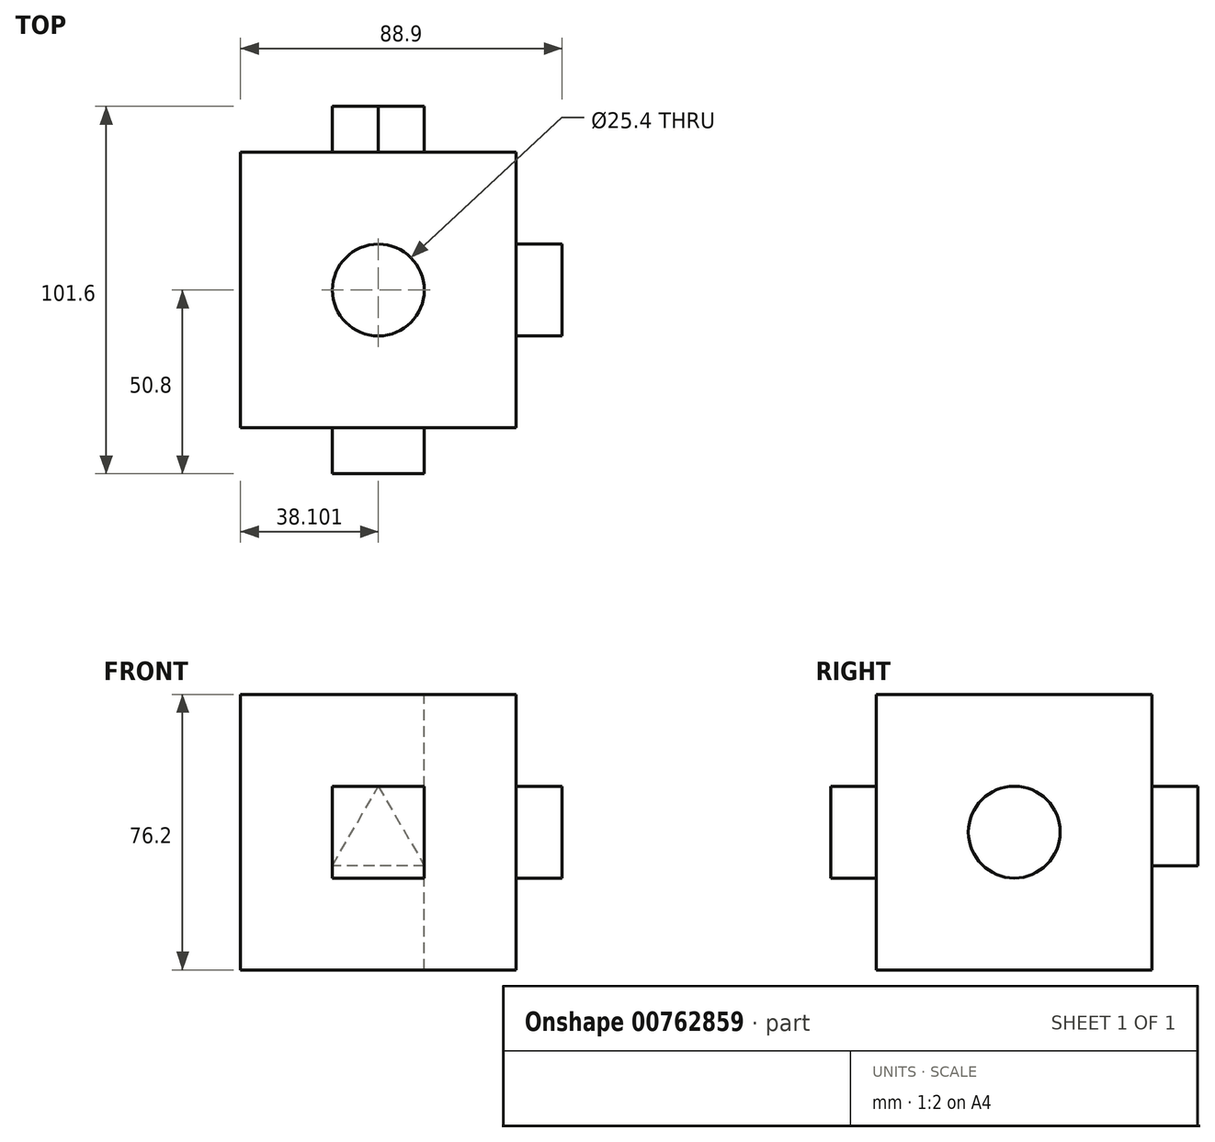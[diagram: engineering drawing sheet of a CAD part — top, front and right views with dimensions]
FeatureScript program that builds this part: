
annotation { "Feature Type Name" : "Feature", "Feature Type Description" : "" }
export const myFeature = defineFeature(function(context is Context, id is Id, definition is map)
    precondition{}
    {
        {
            var Q0;
            Q0=qCreatedBy(makeId("Front.planeOp"),FACE);
            var sketch = newSketch(context, id + "F0", { "sketchPlane" : qUnion([Q0])});
            skLineSegment(sketch, "E0.bottom", {"start": v(-73.54, 74.26) * mm, "end": v(2.66, 74.26) * mm});
            skLineSegment(sketch, "E0.top", {"start": v(-73.54, -1.94) * mm, "end": v(2.66, -1.94) * mm});
            skLineSegment(sketch, "E0.left", {"start": v(-73.54, 74.26) * mm, "end": v(-73.54, -1.94) * mm});
            skLineSegment(sketch, "E0.right", {"start": v(2.66, 74.26) * mm, "end": v(2.66, -1.94) * mm});
            skSolve(sketch);
        }
        {
            var Q0;
            Q0=makeQuery(id+"F0.imprint","IMPRINT",FACE,{"disambiguationData":[TD([[makeQuery(id+"F0.imprint","IMPRINT",EDGE,{"derivedFrom":sQuery(id+"F0.wireOp",EDGE,"E0.bottom")}),-1.0]])]});
            extrude(context, id + "F1", {"entities" : qUnion([Q0]), "depth" : 76.2 * mm, "offsetDistance" : 25.4 * mm});
        }
        {
            var Q0;
            Q0=makeQuery(id+"F1.opExtrude","CAP_FACE",FACE,{"disambiguationData":[OSD([sQuery(id+"F0.wireOp",EDGE,"E0.bottom"),sQuery(id+"F0.wireOp",EDGE,"E0.top"),sQuery(id+"F0.wireOp",EDGE,"E0.left"),sQuery(id+"F0.wireOp",EDGE,"E0.right")])],"isStart":false});
            var sketch = newSketch(context, id + "F2", { "sketchPlane" : qUnion([Q0])});
            skLineSegment(sketch, "E1.bottom", {"start": v(-48.14, 48.86) * mm, "end": v(-22.74, 48.86) * mm});
            skLineSegment(sketch, "E1.top", {"start": v(-48.14, 23.46) * mm, "end": v(-22.74, 23.46) * mm});
            skLineSegment(sketch, "E1.left", {"start": v(-48.14, 48.86) * mm, "end": v(-48.14, 23.46) * mm});
            skLineSegment(sketch, "E1.right", {"start": v(-22.74, 48.86) * mm, "end": v(-22.74, 23.46) * mm});
            skSolve(sketch);
        }
        {
            var Q0;
            Q0=makeQuery(id+"F2.imprint","IMPRINT",FACE,{"disambiguationData":[TD([[makeQuery(id+"F2.imprint","IMPRINT",EDGE,{"derivedFrom":sQuery(id+"F2.wireOp",EDGE,"E1.bottom")}),-1.0]])]});
            extrude(context, id + "F3", {"entities" : qUnion([Q0]), "operationType" : NewBodyOperationType.ADD, "depth" : 12.7 * mm, "offsetDistance" : 25.4 * mm});
        }
        {
            var Q0;
            Q0=makeQuery(id+"F1.opExtrude","SWEPT_FACE",FACE,{"disambiguationData":[OSD([sQuery(id+"F0.wireOp",EDGE,"E0.right")])]});
            var sketch = newSketch(context, id + "F4", { "sketchPlane" : qUnion([Q0])});
            skCircle(sketch, "E2", {"center": v(-38.1, 36.16) * mm, "radius": 12.7 * mm});
            skSolve(sketch);
        }
        {
            var Q0;
            Q0=makeQuery(id+"F4.imprint","IMPRINT",FACE,{"disambiguationData":[TD([[makeQuery(id+"F4.imprint","IMPRINT",EDGE,{"derivedFrom":sQuery(id+"F4.wireOp",EDGE,"E2")}),1.0]])]});
            extrude(context, id + "F5", {"entities" : qUnion([Q0]), "operationType" : NewBodyOperationType.ADD, "depth" : 12.7 * mm, "offsetDistance" : 25.4 * mm});
        }
        {
            var Q0;
            Q0=makeQuery(id+"F1.opExtrude","SWEPT_FACE",FACE,{"disambiguationData":[OSD([sQuery(id+"F0.wireOp",EDGE,"E0.bottom")])]});
            var sketch = newSketch(context, id + "F6", { "sketchPlane" : qUnion([Q0])});
            skPoint(sketch, "E3", {"position": v(-35.44, -38.1) * mm});
            skSolve(sketch);
        }
        {
            var Q0;
            Q0=sQuery(id+"F6.wireOp",VERTEX,"E3");
            var Q1;
            Q1=makeQuery(id+"F1.opExtrude","SWEPT_BODY",BODY,{"disambiguationData":[OSD([sQuery(id+"F0.wireOp",EDGE,"E0.bottom"),sQuery(id+"F0.wireOp",EDGE,"E0.top"),sQuery(id+"F0.wireOp",EDGE,"E0.left"),sQuery(id+"F0.wireOp",EDGE,"E0.right")])]});
            hole(context, id + "F7", {"style" : HoleStyle.SIMPLE, "endStyle" : HoleEndStyle.THROUGH, "holeDiameter" : 25.4 * mm, "majorDiameter" : 6.35 * mm, "isTappedThrough" : true, "tappedDepth" : 12.7 * mm, "tapClearance" : 3, "locations" : qUnion([Q0]), "scope" : qUnion([Q1])});
        }
        {
            var Q0;
            Q0=makeQuery(id+"F1.opExtrude","CAP_FACE",FACE,{"disambiguationData":[OSD([sQuery(id+"F0.wireOp",EDGE,"E0.bottom"),sQuery(id+"F0.wireOp",EDGE,"E0.top"),sQuery(id+"F0.wireOp",EDGE,"E0.left"),sQuery(id+"F0.wireOp",EDGE,"E0.right")])],"isStart":true});
            var sketch = newSketch(context, id + "F8", { "sketchPlane" : qUnion([Q0])});
            skLineSegment(sketch, "E4", {"start": v(35.44, 48.86) * mm, "end": v(22.74, 26.87) * mm});
            skLineSegment(sketch, "E5", {"start": v(22.74, 26.87) * mm, "end": v(48.14, 26.87) * mm});
            skLineSegment(sketch, "E6", {"start": v(48.14, 26.87) * mm, "end": v(35.44, 48.86) * mm});
            skSolve(sketch);
        }
        {
            var Q0;
            Q0=makeQuery(id+"F8.imprint","IMPRINT",FACE,{"disambiguationData":[TD([[makeQuery(id+"F8.imprint","IMPRINT",EDGE,{"derivedFrom":sQuery(id+"F8.wireOp",EDGE,"E4")}),1.0]])]});
            extrude(context, id + "F9", {"entities" : qUnion([Q0]), "operationType" : NewBodyOperationType.ADD, "depth" : 12.7 * mm, "offsetDistance" : 25.4 * mm});
        }
    });
